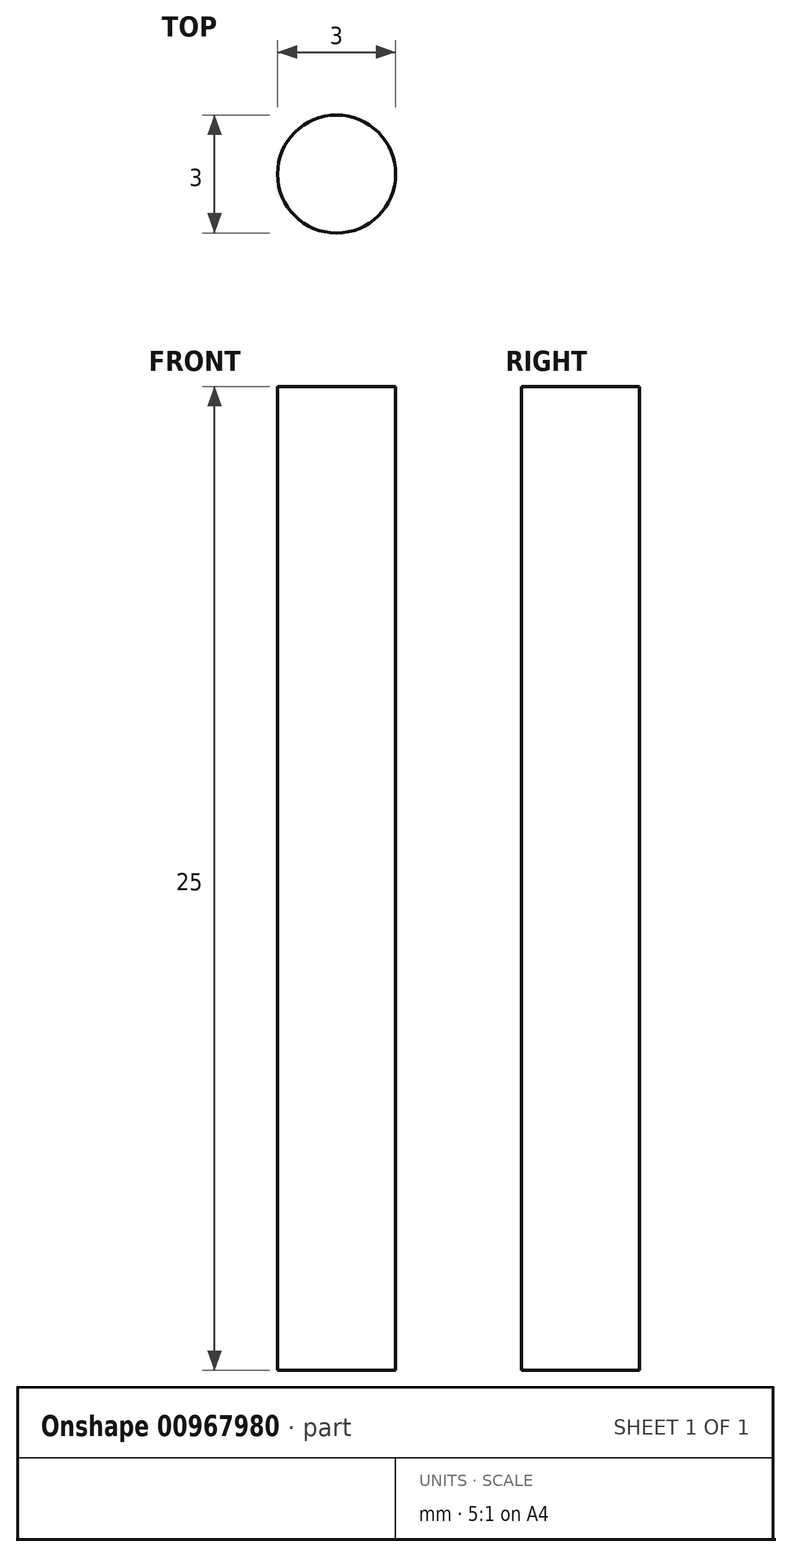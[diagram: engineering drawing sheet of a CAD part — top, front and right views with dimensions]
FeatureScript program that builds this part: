
annotation { "Feature Type Name" : "Feature", "Feature Type Description" : "" }
export const myFeature = defineFeature(function(context is Context, id is Id, definition is map)
    precondition{}
    {
        {
            var Q0;
            Q0=qCreatedBy(makeId("Top.planeOp"),FACE);
            var sketch = newSketch(context, id + "F0", { "sketchPlane" : qUnion([Q0])});
            skCircle(sketch, "E0", {"center": v(0, 0) * mm, "radius": 1.5 * mm});
            skSolve(sketch);
        }
        {
            var Q0;
            Q0 = qSketchRegion(id + "F0", true);
            extrude(context, id + "F1", {"entities" : qUnion([Q0]), "depth" : 25 * mm, "offsetDistance" : 25 * mm});
        }
    });
